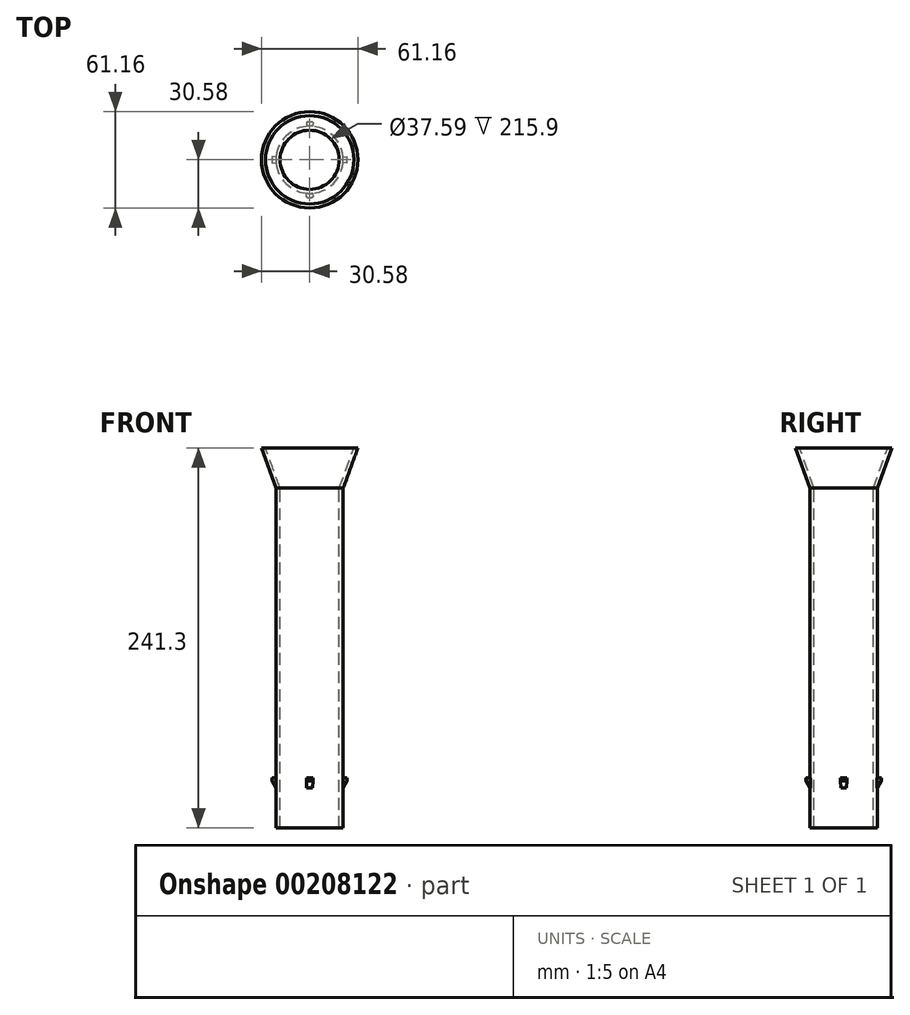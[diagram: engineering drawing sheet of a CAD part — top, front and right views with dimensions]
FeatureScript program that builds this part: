
annotation { "Feature Type Name" : "Feature", "Feature Type Description" : "" }
export const myFeature = defineFeature(function(context is Context, id is Id, definition is map)
    precondition{}
    {
        {
            var Q0;
            Q0=qCreatedBy(makeId("Top.planeOp"),FACE);
            var sketch = newSketch(context, id + "F0", { "sketchPlane" : qUnion([Q0])});
            skCircle(sketch, "E0", {"center": v(0, 0) * mm, "radius": 18.8 * mm});
            skCircle(sketch, "E1", {"center": v(0, 0) * mm, "radius": 21.34 * mm});
            skSolve(sketch);
        }
        {
            var Q0;
            Q0 = qSketchRegion(id + "F0", true);
            extrude(context, id + "F1", {"entities" : qUnion([Q0]), "oppositeDirection" : true, "depth" : 215.9 * mm});
        }
        {
            var Q0;
            Q0=qCreatedBy(makeId("Front.planeOp"),FACE);
            var sketch = newSketch(context, id + "F2", { "sketchPlane" : qUnion([Q0])});
            skLineSegment(sketch, "E2", {"start": v(0, 0) * mm, "end": v(21.34, 0) * mm, "construction": true});
            skLineSegment(sketch, "E3", {"start": v(21.34, 0) * mm, "end": v(18.8, 0) * mm});
            skLineSegment(sketch, "E4", {"start": v(21.34, 0) * mm, "end": v(30.58, 25.4) * mm});
            skLineSegment(sketch, "E5", {"start": v(30.58, 25.4) * mm, "end": v(28.04, 25.4) * mm});
            skLineSegment(sketch, "E6", {"start": v(28.04, 25.4) * mm, "end": v(18.8, 0) * mm});
            skLineSegment(sketch, "E7", {"start": v(0, 0) * mm, "end": v(0, 25.5) * mm, "construction": true});
            skLineSegment(sketch, "E8", {"start": v(18.8, 0) * mm, "end": v(18.8, 22.8) * mm, "construction": true});
            skSolve(sketch);
        }
        {
            var Q0;
            Q0 = qSketchRegion(id + "F2", true);
            var Q1;
            Q1=sQuery(id+"F2.wireOp",EDGE,"E7");
            revolve(context, id + "F3", {"operationType" : NewBodyOperationType.ADD, "entities" : qUnion([Q0]), "axis" : qUnion([Q1]), "revolveType" : RevolveType.FULL});
        }
        {
            var Q0;
            Q0=qCreatedBy(makeId("Top.planeOp"),FACE);
            var sketch = newSketch(context, id + "F4", { "sketchPlane" : qUnion([Q0])});
            skLineSegment(sketch, "E9", {"start": v(0, 0) * mm, "end": v(0, 51.69) * mm, "construction": true});
            skLineSegment(sketch, "E10", {"start": v(0, 0) * mm, "end": v(0, -45.28) * mm, "construction": true});
            skLineSegment(sketch, "E11", {"start": v(0, 0) * mm, "end": v(60.03, 0) * mm, "construction": true});
            skLineSegment(sketch, "E12", {"start": v(0, 0) * mm, "end": v(-51.83, 0) * mm, "construction": true});
            skLineSegment(sketch, "E13", {"start": v(0, 0) * mm, "end": v(-52.94, 4.63) * mm, "construction": true});
            skLineSegment(sketch, "E14", {"start": v(0, 0) * mm, "end": v(-4.14, 47.34) * mm, "construction": true});
            skLineSegment(sketch, "E15", {"start": v(0, 0) * mm, "end": v(4.23, 48.4) * mm, "construction": true});
            skLineSegment(sketch, "E16", {"start": v(0, 0) * mm, "end": v(52.82, 4.62) * mm, "construction": true});
            skLineSegment(sketch, "E17", {"start": v(0, 0) * mm, "end": v(56.41, -4.94) * mm, "construction": true});
            skLineSegment(sketch, "E18", {"start": v(0, 0) * mm, "end": v(3.82, -43.63) * mm, "construction": true});
            skLineSegment(sketch, "E19", {"start": v(0, 0) * mm, "end": v(-3.39, -38.73) * mm, "construction": true});
            skLineSegment(sketch, "E20", {"start": v(0, 0) * mm, "end": v(-45.63, -4) * mm, "construction": true});
            skArc(sketch, "E21", {"start": v(-21.25, -1.86) * mm, "mid": v(-21.34, 0) * mm, "end": v(-21.25, 1.86) * mm});
            skArc(sketch, "E22", {"start": v(-1.86, 21.25) * mm, "mid": v(0, 21.34) * mm, "end": v(1.86, 21.25) * mm});
            skArc(sketch, "E23", {"start": v(21.25, 1.86) * mm, "mid": v(21.34, 0) * mm, "end": v(21.25, -1.86) * mm});
            skArc(sketch, "E24", {"start": v(1.86, -21.25) * mm, "mid": v(0, -21.34) * mm, "end": v(-1.86, -21.25) * mm});
            skArc(sketch, "E25", {"start": v(-23.79, -2.08) * mm, "mid": v(-23.88, 0) * mm, "end": v(-23.79, 2.08) * mm});
            skArc(sketch, "E26", {"start": v(-2.08, 23.79) * mm, "mid": v(0, 23.88) * mm, "end": v(2.08, 23.79) * mm});
            skArc(sketch, "E27", {"start": v(23.79, 2.08) * mm, "mid": v(23.88, 0) * mm, "end": v(23.79, -2.08) * mm});
            skArc(sketch, "E28", {"start": v(2.08, -23.79) * mm, "mid": v(0, -23.88) * mm, "end": v(-2.08, -23.79) * mm});
            skLineSegment(sketch, "E29", {"start": v(-21.25, 1.86) * mm, "end": v(-23.79, 2.08) * mm});
            skLineSegment(sketch, "E30", {"start": v(-23.79, -2.08) * mm, "end": v(-21.25, -1.86) * mm});
            skLineSegment(sketch, "E31", {"start": v(-2.08, 23.79) * mm, "end": v(-1.86, 21.25) * mm});
            skLineSegment(sketch, "E32", {"start": v(2.08, 23.79) * mm, "end": v(1.86, 21.25) * mm});
            skLineSegment(sketch, "E33", {"start": v(21.25, 1.86) * mm, "end": v(23.79, 2.08) * mm});
            skLineSegment(sketch, "E34", {"start": v(23.79, -2.08) * mm, "end": v(21.25, -1.86) * mm});
            skLineSegment(sketch, "E35", {"start": v(1.86, -21.25) * mm, "end": v(2.08, -23.79) * mm});
            skLineSegment(sketch, "E36", {"start": v(-2.08, -23.79) * mm, "end": v(-1.86, -21.25) * mm});
            skLineSegment(sketch, "E37", {"start": v(-21.34, 0) * mm, "end": v(-23.88, 0) * mm, "construction": true});
            skLineSegment(sketch, "E38", {"start": v(0, 21.34) * mm, "end": v(0, 23.88) * mm, "construction": true});
            skLineSegment(sketch, "E39", {"start": v(21.34, 0) * mm, "end": v(23.88, 0) * mm, "construction": true});
            skLineSegment(sketch, "E40", {"start": v(0, -21.34) * mm, "end": v(0, -23.88) * mm, "construction": true});
            skSolve(sketch);
        }
        {
            var Q0;
            Q0 = qSketchRegion(id + "F4", true);
            extrude(context, id + "F5", {"entities" : qUnion([Q0]), "operationType" : NewBodyOperationType.ADD, "oppositeDirection" : true, "depth" : 190.5 * mm, "hasSecondDirection" : true, "secondDirectionOppositeDirection" : true, "secondDirectionDepth" : 184.15 * mm});
        }
        {
            var Q0;
            Q0=qCreatedBy(makeId("Front.planeOp"),FACE);
            var sketch = newSketch(context, id + "F6", { "sketchPlane" : qUnion([Q0])});
            skLineSegment(sketch, "E41", {"start": v(0, 0) * mm, "end": v(21.34, 0) * mm, "construction": true});
            skLineSegment(sketch, "E42", {"start": v(21.34, 0) * mm, "end": v(21.34, -190.5) * mm, "construction": true});
            skLineSegment(sketch, "E43", {"start": v(21.34, -190.5) * mm, "end": v(21.34, -184.15) * mm, "construction": true});
            skLineSegment(sketch, "E44", {"start": v(21.34, -184.15) * mm, "end": v(23.88, -184.15) * mm});
            skLineSegment(sketch, "E45", {"start": v(23.88, -184.15) * mm, "end": v(23.88, -186.1) * mm});
            skLineSegment(sketch, "E46", {"start": v(23.88, -186.1) * mm, "end": v(21.34, -190.5) * mm});
            skLineSegment(sketch, "E47", {"start": v(21.34, -184.15) * mm, "end": v(21.34, -190.5) * mm});
            skLineSegment(sketch, "E48", {"start": v(0, 0) * mm, "end": v(0, -166.36) * mm, "construction": true});
            skLineSegment(sketch, "E49", {"start": v(21.34, -190.5) * mm, "end": v(23.88, -190.5) * mm});
            skLineSegment(sketch, "E50", {"start": v(23.88, -190.5) * mm, "end": v(23.88, -186.1) * mm});
            skSolve(sketch);
        }
        {
            var Q0;
            Q0=makeQuery(id+"F6.imprint","IMPRINT",FACE,{"disambiguationData":[TD([[makeQuery(id+"F6.imprint","IMPRINT",EDGE,{"derivedFrom":sQuery(id+"F6.wireOp",EDGE,"E46")}),1.0]])]});
            var Q1;
            Q1=sQuery(id+"F6.wireOp",EDGE,"E48");
            revolve(context, id + "F7", {"operationType" : NewBodyOperationType.REMOVE, "entities" : qUnion([Q0]), "axis" : qUnion([Q1]), "revolveType" : RevolveType.FULL, "oppositeDirection" : true});
        }
    });
